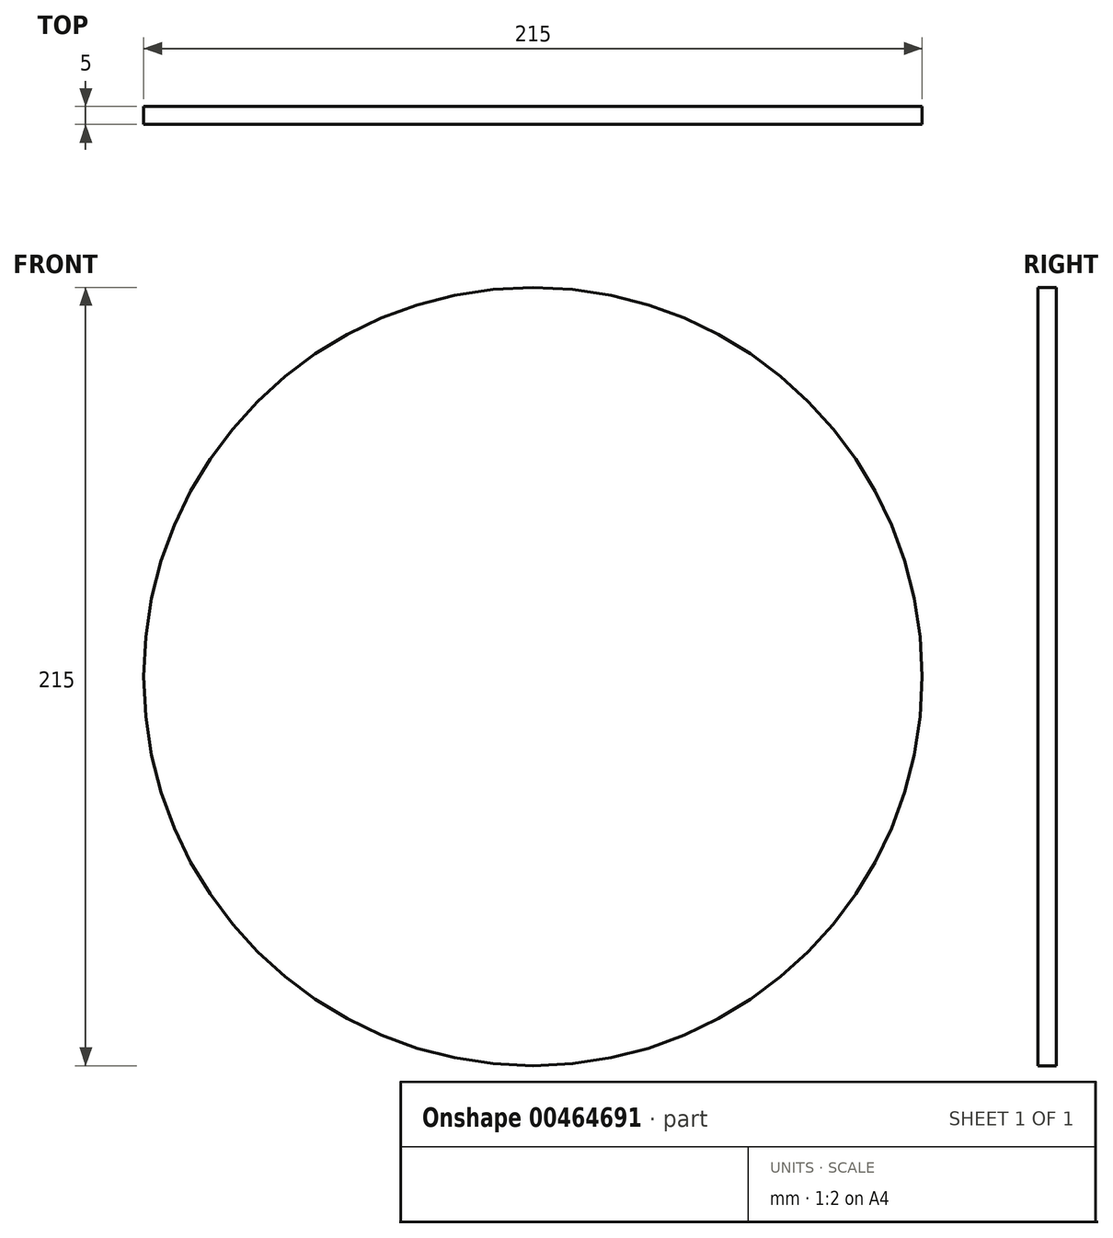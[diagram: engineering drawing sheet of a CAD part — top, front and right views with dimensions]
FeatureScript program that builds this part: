
annotation { "Feature Type Name" : "Feature", "Feature Type Description" : "" }
export const myFeature = defineFeature(function(context is Context, id is Id, definition is map)
    precondition{}
    {
        {
            var Q0;
            Q0=qCreatedBy(makeId("Front.planeOp"),FACE);
            var sketch = newSketch(context, id + "F0", { "sketchPlane" : qUnion([Q0])});
            skCircle(sketch, "E0", {"center": v(0, 0) * mm, "radius": 95 * mm, "construction": true});
            skCircle(sketch, "E1", {"center": v(0, 0) * mm, "radius": 105 * mm, "construction": true});
            skLineSegment(sketch, "E2", {"start": v(0, 0) * mm, "end": v(0, 105) * mm, "construction": true});
            skLineSegment(sketch, "E3.1.0", {"start": v(0, 0) * mm, "end": v(-67.5, 80.43) * mm, "construction": true});
            skLineSegment(sketch, "E3.2.0", {"start": v(0, 0) * mm, "end": v(-103.4, 18.23) * mm, "construction": true});
            skLineSegment(sketch, "E3.3.0", {"start": v(0, 0) * mm, "end": v(-90.93, -52.5) * mm, "construction": true});
            skLineSegment(sketch, "E3.4.0", {"start": v(0, 0) * mm, "end": v(-35.91, -98.67) * mm, "construction": true});
            skLineSegment(sketch, "E3.5.0", {"start": v(0, 0) * mm, "end": v(35.91, -98.67) * mm, "construction": true});
            skLineSegment(sketch, "E3.6.0", {"start": v(0, 0) * mm, "end": v(90.93, -52.5) * mm, "construction": true});
            skLineSegment(sketch, "E3.7.0", {"start": v(0, 0) * mm, "end": v(103.4, 18.23) * mm, "construction": true});
            skLineSegment(sketch, "E3.8.0", {"start": v(0, 0) * mm, "end": v(67.5, 80.43) * mm, "construction": true});
            skCircle(sketch, "E4", {"center": v(0, 0) * mm, "radius": 47.5 * mm, "construction": true});
            skCircle(sketch, "E5", {"center": v(0, 0) * mm, "radius": 55 * mm, "construction": true});
            skCircle(sketch, "E6", {"center": v(0, 0) * mm, "radius": 107.5 * mm});
            skSolve(sketch);
        }
        {
            var Q0;
            Q0=qSketchRegion(id+"F0",true);
            extrude(context, id + "F1", {"entities" : qUnion([Q0]), "depth" : 5 * mm});
        }
    });
